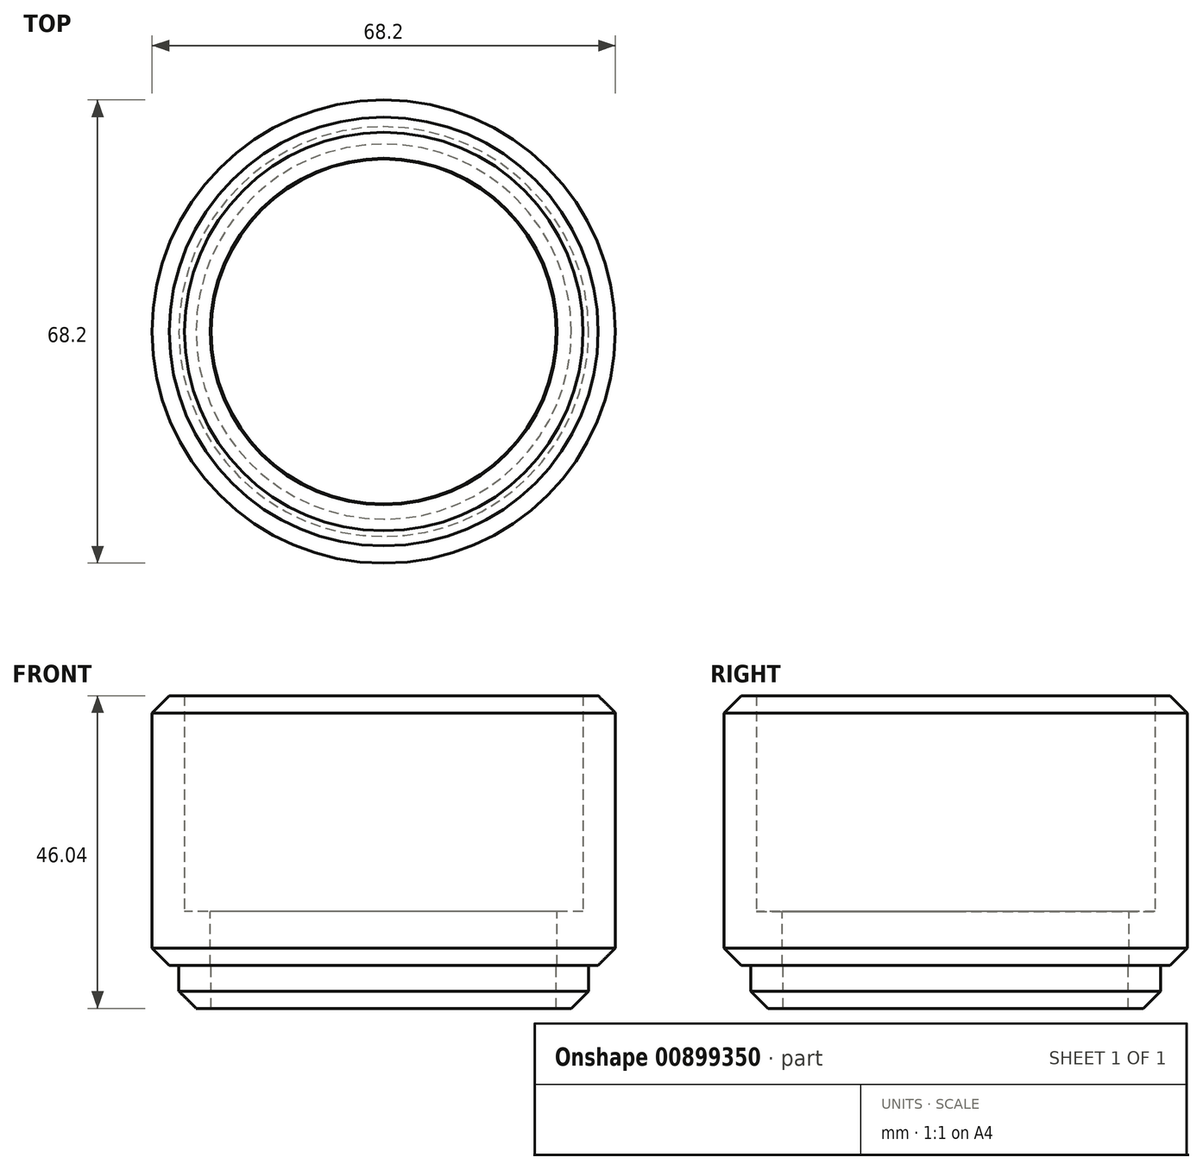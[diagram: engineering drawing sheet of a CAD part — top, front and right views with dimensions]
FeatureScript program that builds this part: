
annotation { "Feature Type Name" : "Feature", "Feature Type Description" : "" }
export const myFeature = defineFeature(function(context is Context, id is Id, definition is map)
    precondition{}
    {
        {
            var Q0;
            Q0=qCreatedBy(makeId("Top.planeOp"),FACE);
            var sketch = newSketch(context, id + "F0", { "sketchPlane" : qUnion([Q0])});
            skCircle(sketch, "E0", {"center": v(0, 0) * mm, "radius": 29.34 * mm});
            skCircle(sketch, "E1.0", {"center": v(0, 0) * mm, "radius": 34.1 * mm});
            skCircle(sketch, "E2.0", {"center": v(0, 0) * mm, "radius": 25.53 * mm});
            skSolve(sketch);
        }
        {
            var Q0;
            Q0=makeQuery(id+"F0.imprint","IMPRINT",FACE,{"disambiguationData":[TD([[makeQuery(id+"F0.imprint","IMPRINT",EDGE,{"derivedFrom":sQuery(id+"F0.wireOp",EDGE,"E0")}),-1.0]])]});
            extrude(context, id + "F1", {"entities" : qUnion([Q0]), "depth" : 31.75 * mm});
        }
        {
            var Q0;
            Q0=makeQuery(id+"F0.imprint","IMPRINT",FACE,{"disambiguationData":[TD([[makeQuery(id+"F0.imprint","IMPRINT",EDGE,{"derivedFrom":sQuery(id+"F0.wireOp",EDGE,"E0")}),1.0]])]});
            var Q1;
            Q1=makeQuery(id+"F0.imprint","IMPRINT",FACE,{"disambiguationData":[TD([[makeQuery(id+"F0.imprint","IMPRINT",EDGE,{"derivedFrom":sQuery(id+"F0.wireOp",EDGE,"E0")}),-1.0]])]});
            extrude(context, id + "F2", {"entities" : qUnion([Q0, Q1]), "operationType" : NewBodyOperationType.ADD, "oppositeDirection" : true, "depth" : 7.94 * mm});
        }
        {
            var Q0;
            Q0=makeQuery(id+"F2.opExtrude","CAP_FACE",FACE,{"disambiguationData":[OSD([sQuery(id+"F0.wireOp",EDGE,"E1.0"),sQuery(id+"F0.wireOp",EDGE,"E2.0")])],"isStart":false});
            var sketch = newSketch(context, id + "F3", { "sketchPlane" : qUnion([Q0])});
            skCircle(sketch, "E3", {"center": v(0, 0) * mm, "radius": 25.4 * mm});
            skCircle(sketch, "E4.0", {"center": v(0, 0) * mm, "radius": 30.16 * mm});
            skSolve(sketch);
        }
        {
            var Q0;
            Q0=qSketchRegion(id+"F3",true);
            extrude(context, id + "F4", {"entities" : qUnion([Q0]), "operationType" : NewBodyOperationType.ADD, "depth" : 6.35 * mm});
        }
        {
            var Q0;
            Q0=makeQuery(id+"F1.opExtrude","CAP_EDGE",EDGE,{"disambiguationData":[OSD([sQuery(id+"F0.wireOp",EDGE,"E1.0")])],"isStart":false});
            var Q1;
            Q1=makeQuery(id+"F2.opExtrude","CAP_EDGE",EDGE,{"disambiguationData":[OSD([sQuery(id+"F0.wireOp",EDGE,"E1.0")])],"isStart":false});
            var Q2;
            Q2=makeQuery(id+"F4.opExtrude","CAP_EDGE",EDGE,{"disambiguationData":[OSD([sQuery(id+"F3.wireOp",EDGE,"E4.0")])],"isStart":false});
            chamfer(context, id + "F5", {"entities" : qUnion([Q0, Q1, Q2]), "width" : 2.54 * mm, "tangentPropagation" : true});
        }
    });
